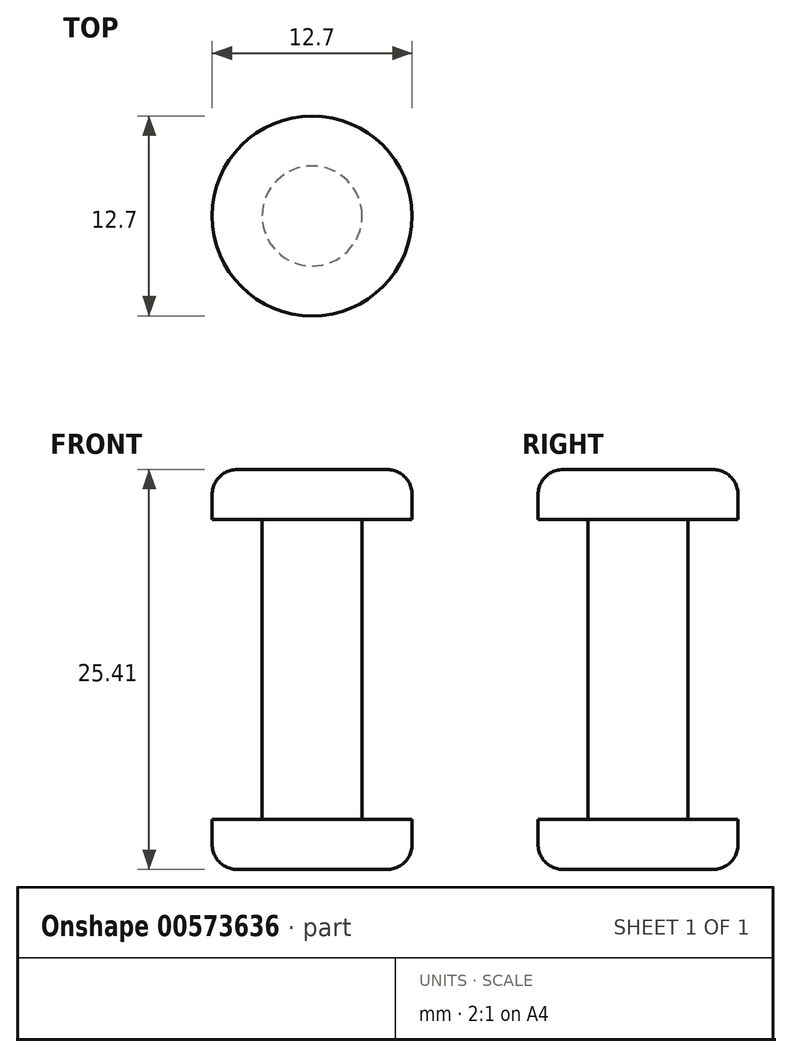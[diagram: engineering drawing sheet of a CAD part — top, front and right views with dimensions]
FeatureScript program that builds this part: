
annotation { "Feature Type Name" : "Feature", "Feature Type Description" : "" }
export const myFeature = defineFeature(function(context is Context, id is Id, definition is map)
    precondition{}
    {
        {
            var Q0;
            Q0=qCreatedBy(makeId("Front.planeOp"),FACE);
            var sketch = newSketch(context, id + "F0", { "sketchPlane" : qUnion([Q0])});
            skLineSegment(sketch, "E0", {"start": v(0, 0) * mm, "end": v(0, 19.05) * mm});
            skLineSegment(sketch, "E1.0", {"start": v(-3.18, 0) * mm, "end": v(-3.18, 19.05) * mm});
            skLineSegment(sketch, "E2", {"start": v(-3.18, 0) * mm, "end": v(-6.35, 0) * mm});
            skLineSegment(sketch, "E3", {"start": v(0, 9.53) * mm, "end": v(6.15, 9.53) * mm, "construction": true});
            skPoint(sketch, "E3.endSnap0", {"position": v(0, 9.53) * mm});
            skLineSegment(sketch, "E4.MirrorCS", {"start": v(-3.18, 19.05) * mm, "end": v(-6.35, 19.05) * mm});
            skLineSegment(sketch, "E5", {"start": v(-6.35, 0) * mm, "end": v(-6.35, -3.18) * mm});
            skLineSegment(sketch, "E6", {"start": v(-6.35, -3.18) * mm, "end": v(0, -3.17) * mm});
            skLineSegment(sketch, "E7", {"start": v(0, -3.17) * mm, "end": v(0, 0) * mm});
            skLineSegment(sketch, "E8.MirrorCS", {"start": v(-6.35, 22.23) * mm, "end": v(0, 22.23) * mm});
            skLineSegment(sketch, "E9.MirrorCS", {"start": v(-6.35, 19.05) * mm, "end": v(-6.35, 22.23) * mm});
            skLineSegment(sketch, "E10.MirrorCS", {"start": v(0, 22.23) * mm, "end": v(0, 19.05) * mm});
            skSolve(sketch);
        }
        {
            var Q0;
            Q0=makeQuery(id+"F0.imprint","IMPRINT",FACE,{"disambiguationData":[TD([[makeQuery(id+"F0.imprint","IMPRINT",EDGE,{"derivedFrom":sQuery(id+"F0.wireOp",EDGE,"E0")}),1.0]])]});
            var Q1;
            Q1=sQuery(id+"F0.wireOp",EDGE,"E0");
            revolve(context, id + "F1", {"entities" : qUnion([Q0]), "axis" : qUnion([Q1]), "revolveType" : RevolveType.FULL});
        }
        {
            var Q0;
            Q0=makeQuery(id+"F1.opRevolve","SWEPT_FACE",FACE,{"disambiguationData":[OSD([sQuery(id+"F0.wireOp",EDGE,"E8.MirrorCS")])]});
            var Q1;
            Q1=makeQuery(id+"F1.opRevolve","SWEPT_FACE",FACE,{"disambiguationData":[OSD([sQuery(id+"F0.wireOp",EDGE,"E6")])]});
            fillet(context, id + "F2", {"entities" : qUnion([Q0, Q1]), "radius" : 1.59 * mm, "tangentPropagation" : true, "allowEdgeOverflow" : false});
        }
    });
